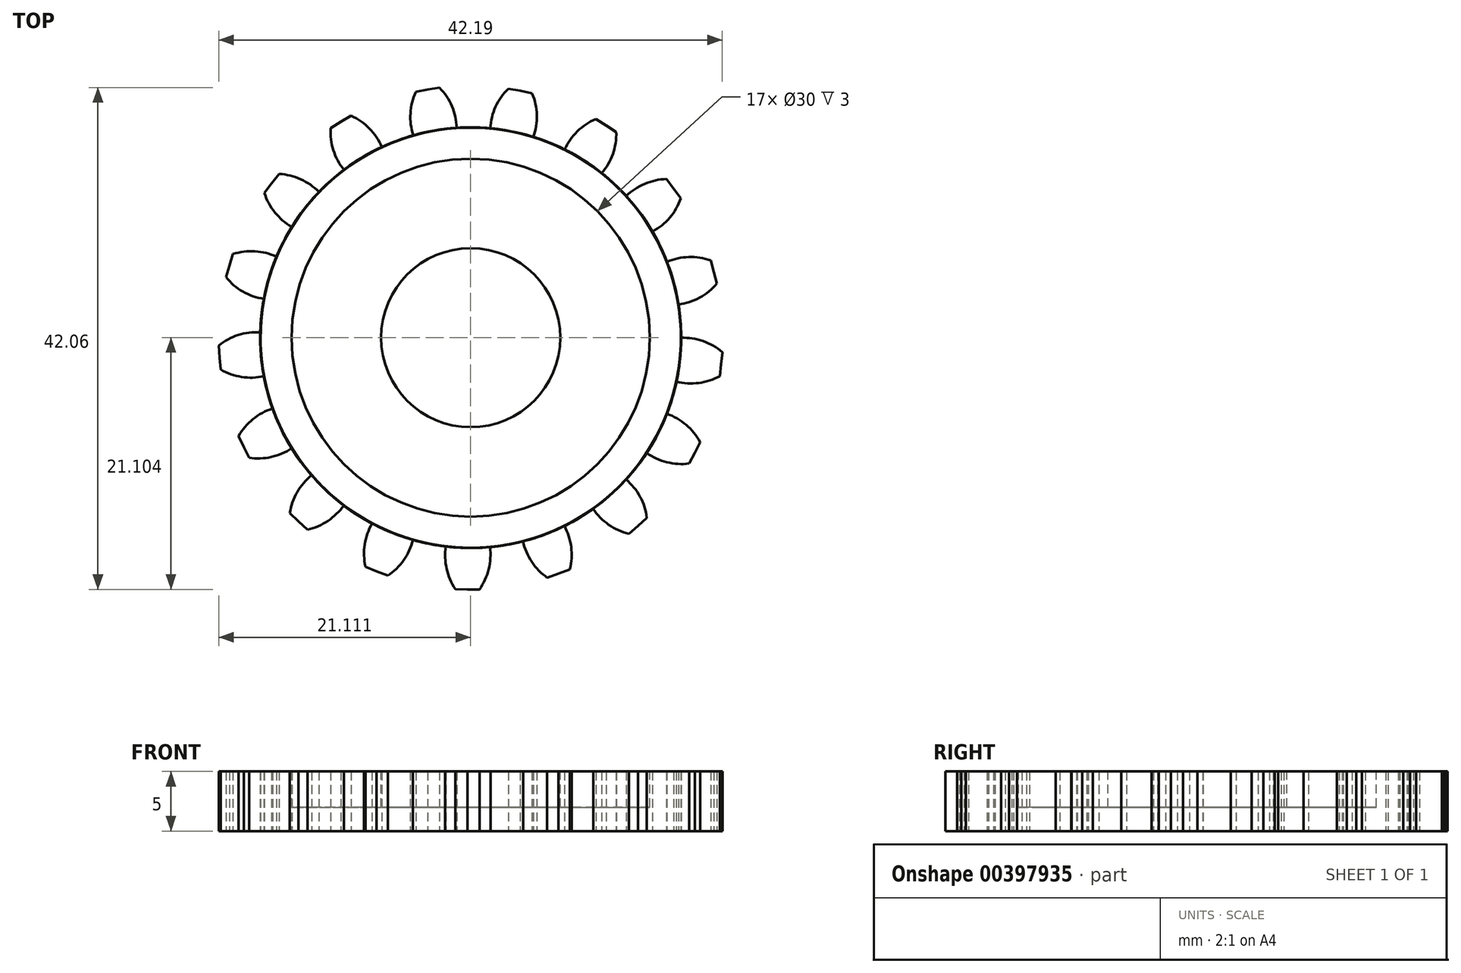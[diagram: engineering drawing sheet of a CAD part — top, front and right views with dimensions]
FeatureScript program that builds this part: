
annotation { "Feature Type Name" : "Feature", "Feature Type Description" : "" }
export const myFeature = defineFeature(function(context is Context, id is Id, definition is map)
    precondition{}
    {
        {
            var Q0;
            Q0=qCreatedBy(makeId("Top.planeOp"),FACE);
            var sketch = newSketch(context, id + "F0", { "sketchPlane" : qUnion([Q0])});
            skCircle(sketch, "E0", {"center": v(20.43, 3.16) * mm, "radius": 17.63 * mm});
            skLineSegment(sketch, "E1", {"start": v(20.43, 3.16) * mm, "end": v(24.58, 23.85) * mm});
            skArc(sketch, "E2", {"start": v(23.6, 24.04) * mm, "mid": v(22.52, 22.52) * mm, "end": v(22.07, 20.71) * mm});
            skLineSegment(sketch, "E3", {"start": v(23.6, 24.04) * mm, "end": v(24.58, 23.85) * mm});
            skLineSegment(sketch, "E4.MirrorCS", {"start": v(25.57, 23.65) * mm, "end": v(24.58, 23.85) * mm});
            skArc(sketch, "E5.MirrorCS", {"start": v(25.57, 23.65) * mm, "mid": v(25.97, 21.83) * mm, "end": v(25.7, 19.99) * mm});
            skSolve(sketch);
        }
        {
            var Q0;
            Q0 = qSketchRegion(id + "F0", true);
            extrude(context, id + "F1", {"entities" : qUnion([Q0]), "depth" : 5 * mm});
        }
        {
            var Q0;
            Q0=makeQuery(id+"F1.opExtrude","CAP_FACE",FACE,{"disambiguationData":[OSD([sQuery(id+"F0.wireOp",EDGE,"E0"),sQuery(id+"F0.wireOp",EDGE,"E2"),sQuery(id+"F0.wireOp",EDGE,"E3"),sQuery(id+"F0.wireOp",EDGE,"E4.MirrorCS"),sQuery(id+"F0.wireOp",EDGE,"E5.MirrorCS")])],"isStart":false});
            var sketch = newSketch(context, id + "F2", { "sketchPlane" : qUnion([Q0])});
            skArc(sketch, "E6.0.0", {"start": v(22.07, 20.71) * mm, "mid": v(16.96, -14.12) * mm, "end": v(25.7, 19.99) * mm});
            skArc(sketch, "E6.0.1", {"start": v(25.7, 19.99) * mm, "mid": v(25.97, 21.83) * mm, "end": v(25.57, 23.65) * mm});
            skLineSegment(sketch, "E6.0.2", {"start": v(25.57, 23.65) * mm, "end": v(24.58, 23.85) * mm});
            skLineSegment(sketch, "E6.0.3", {"start": v(24.58, 23.85) * mm, "end": v(23.6, 24.04) * mm});
            skArc(sketch, "E6.0.4", {"start": v(23.6, 24.04) * mm, "mid": v(22.52, 22.52) * mm, "end": v(22.07, 20.71) * mm});
            skCircle(sketch, "E7", {"center": v(20.43, 3.16) * mm, "radius": 7.5 * mm});
            skCircle(sketch, "E8", {"center": v(20.43, 3.16) * mm, "radius": 15 * mm});
            skSolve(sketch);
        }
        {
            var Q0;
            Q0=makeQuery(id+"F2.imprint","IMPRINT",FACE,{"disambiguationData":[TD([[makeQuery(id+"F2.imprint","IMPRINT",EDGE,{"derivedFrom":sQuery(id+"F2.wireOp",EDGE,"E7")}),-1.0]])]});
            extrude(context, id + "F3", {"entities" : qUnion([Q0]), "operationType" : NewBodyOperationType.REMOVE, "oppositeDirection" : true, "depth" : 3 * mm});
        }
        {
            var Q0;
            Q0=makeQuery(id+"F1.opExtrude","SWEPT_BODY",BODY,{"disambiguationData":[OSD([sQuery(id+"F0.wireOp",EDGE,"E0"),sQuery(id+"F0.wireOp",EDGE,"E2"),sQuery(id+"F0.wireOp",EDGE,"E3"),sQuery(id+"F0.wireOp",EDGE,"E4.MirrorCS"),sQuery(id+"F0.wireOp",EDGE,"E5.MirrorCS")])]});
            var Q1;
            Q1=makeQuery(id+"F1.opExtrude","SWEPT_FACE",FACE,{"disambiguationData":[OSD([sQuery(id+"F0.wireOp",EDGE,"E0")])]});
            circularPattern(context, id + "F4", {"entities" : qUnion([Q0]), "axis" : qUnion([Q1]), "angle" : 360 * degree, "instanceCount" : 17, "equalSpace" : true});
        }
    });
